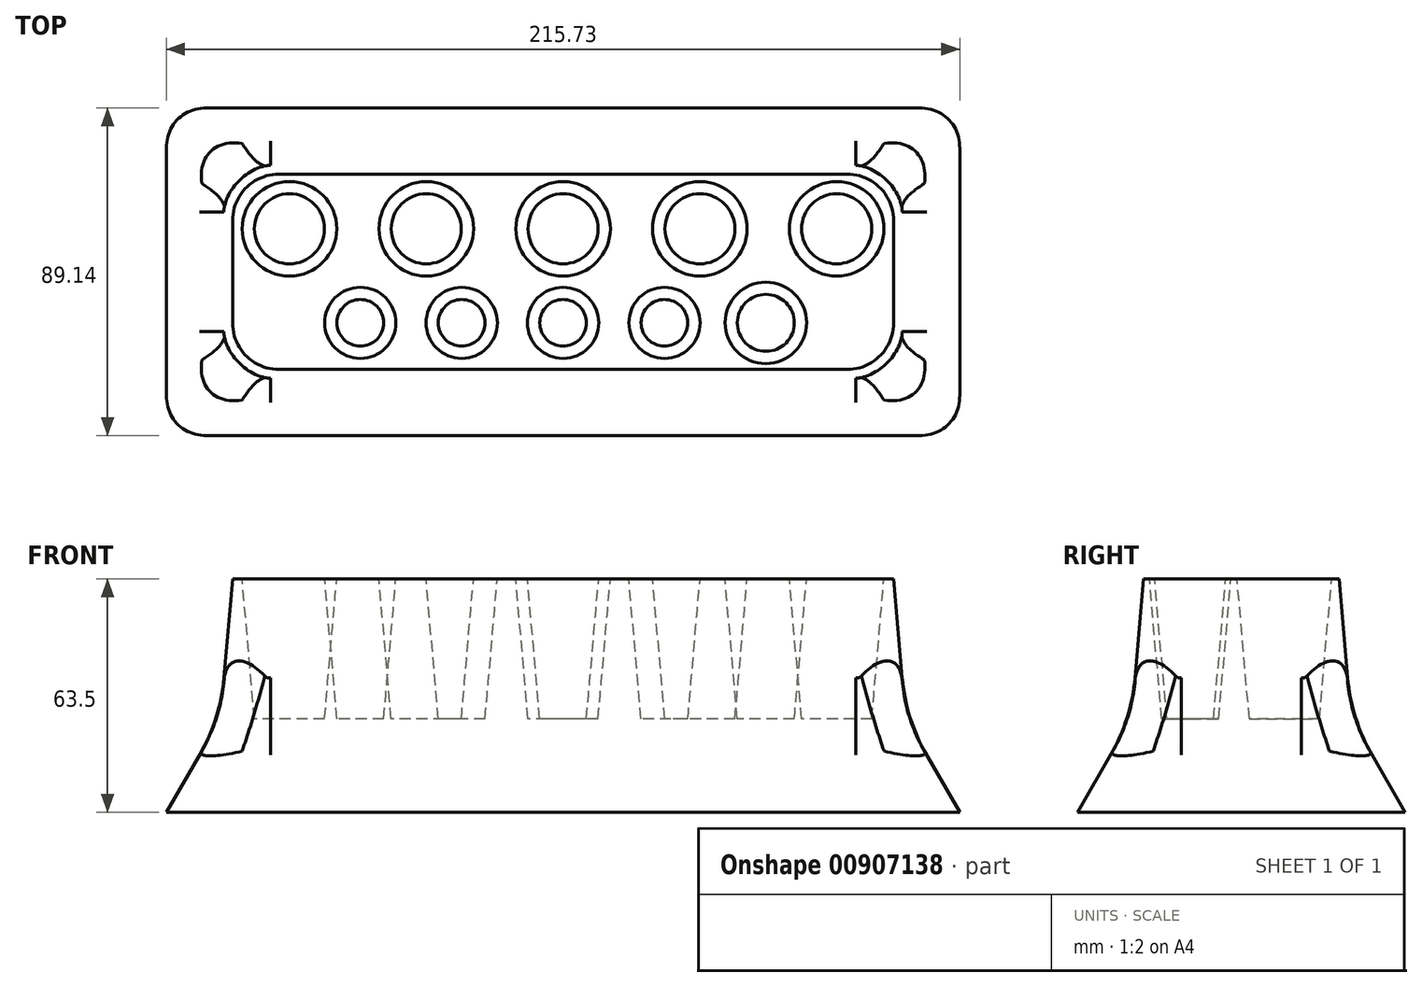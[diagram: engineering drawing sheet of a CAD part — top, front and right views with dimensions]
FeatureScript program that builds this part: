
annotation { "Feature Type Name" : "Feature", "Feature Type Description" : "" }
export const myFeature = defineFeature(function(context is Context, id is Id, definition is map)
    precondition{}
    {
        {
            var Q0;
            Q0=qCreatedBy(makeId("Top.planeOp"),FACE);
            var sketch = newSketch(context, id + "F0", { "sketchPlane" : qUnion([Q0])});
            skLineSegment(sketch, "E0.bottom", {"start": v(0, 0) * mm, "end": v(186.41, 0) * mm});
            skLineSegment(sketch, "E0.top", {"start": v(0, 59.81) * mm, "end": v(186.41, 59.81) * mm});
            skLineSegment(sketch, "E0.left", {"start": v(0, 0) * mm, "end": v(0, 59.81) * mm});
            skLineSegment(sketch, "E0.right", {"start": v(186.41, 0) * mm, "end": v(186.41, 59.81) * mm});
            skCircle(sketch, "E1", {"center": v(18.8, 41.6) * mm, "radius": 9.53 * mm});
            skCircle(sketch, "E2", {"center": v(56, 41.6) * mm, "radius": 9.53 * mm});
            skCircle(sketch, "E3", {"center": v(93.2, 41.6) * mm, "radius": 9.53 * mm});
            skCircle(sketch, "E4", {"center": v(130.4, 41.6) * mm, "radius": 9.53 * mm});
            skCircle(sketch, "E5", {"center": v(167.6, 41.6) * mm, "radius": 9.53 * mm});
            skCircle(sketch, "E6", {"center": v(38.08, 16) * mm, "radius": 6.35 * mm});
            skCircle(sketch, "E7", {"center": v(65.64, 16) * mm, "radius": 6.35 * mm});
            skCircle(sketch, "E8", {"center": v(93.2, 16) * mm, "radius": 6.35 * mm});
            skCircle(sketch, "E9", {"center": v(120.77, 16) * mm, "radius": 6.35 * mm});
            skCircle(sketch, "E10", {"center": v(148.33, 16) * mm, "radius": 7.75 * mm});
            skLineSegment(sketch, "E11", {"start": v(18.8, 41.6) * mm, "end": v(56, 41.6) * mm, "construction": true});
            skLineSegment(sketch, "E12", {"start": v(93.2, 41.6) * mm, "end": v(130.4, 41.6) * mm, "construction": true});
            skLineSegment(sketch, "E13", {"start": v(167.6, 41.6) * mm, "end": v(130.4, 41.6) * mm, "construction": true});
            skLineSegment(sketch, "E14", {"start": v(93.2, 41.6) * mm, "end": v(56, 41.6) * mm, "construction": true});
            skLineSegment(sketch, "E15", {"start": v(38.08, 16) * mm, "end": v(65.64, 16) * mm, "construction": true});
            skLineSegment(sketch, "E16", {"start": v(65.64, 16) * mm, "end": v(93.2, 16) * mm, "construction": true});
            skLineSegment(sketch, "E17", {"start": v(93.2, 16) * mm, "end": v(120.77, 16) * mm, "construction": true});
            skLineSegment(sketch, "E18", {"start": v(120.77, 16) * mm, "end": v(148.33, 16) * mm, "construction": true});
            skLineSegment(sketch, "E19", {"start": v(93.2, 41.6) * mm, "end": v(93.2, 16) * mm, "construction": true});
            skLineSegment(sketch, "E20", {"start": v(93.2, 0) * mm, "end": v(93.2, 16) * mm, "construction": true});
            skSolve(sketch);
        }
        {
            var Q0;
            Q0=makeQuery(id+"F0.imprint","IMPRINT",FACE,{"disambiguationData":[TD([[makeQuery(id+"F0.imprint","IMPRINT",EDGE,{"derivedFrom":sQuery(id+"F0.wireOp",EDGE,"E5")}),1.0]])]});
            var Q1;
            Q1=makeQuery(id+"F0.imprint","IMPRINT",FACE,{"disambiguationData":[TD([[makeQuery(id+"F0.imprint","IMPRINT",EDGE,{"derivedFrom":sQuery(id+"F0.wireOp",EDGE,"E0.bottom")}),1.0]])]});
            var Q2;
            Q2=makeQuery(id+"F0.imprint","IMPRINT",FACE,{"disambiguationData":[TD([[makeQuery(id+"F0.imprint","IMPRINT",EDGE,{"derivedFrom":sQuery(id+"F0.wireOp",EDGE,"E4")}),1.0]])]});
            var Q3;
            Q3=makeQuery(id+"F0.imprint","IMPRINT",FACE,{"disambiguationData":[TD([[makeQuery(id+"F0.imprint","IMPRINT",EDGE,{"derivedFrom":sQuery(id+"F0.wireOp",EDGE,"E10")}),1.0]])]});
            var Q4;
            Q4=makeQuery(id+"F0.imprint","IMPRINT",FACE,{"disambiguationData":[TD([[makeQuery(id+"F0.imprint","IMPRINT",EDGE,{"derivedFrom":sQuery(id+"F0.wireOp",EDGE,"E9")}),1.0]])]});
            var Q5;
            Q5=makeQuery(id+"F0.imprint","IMPRINT",FACE,{"disambiguationData":[TD([[makeQuery(id+"F0.imprint","IMPRINT",EDGE,{"derivedFrom":sQuery(id+"F0.wireOp",EDGE,"E3")}),1.0]])]});
            var Q6;
            Q6=makeQuery(id+"F0.imprint","IMPRINT",FACE,{"disambiguationData":[TD([[makeQuery(id+"F0.imprint","IMPRINT",EDGE,{"derivedFrom":sQuery(id+"F0.wireOp",EDGE,"E8")}),1.0]])]});
            var Q7;
            Q7=makeQuery(id+"F0.imprint","IMPRINT",FACE,{"disambiguationData":[TD([[makeQuery(id+"F0.imprint","IMPRINT",EDGE,{"derivedFrom":sQuery(id+"F0.wireOp",EDGE,"E2")}),1.0]])]});
            var Q8;
            Q8=makeQuery(id+"F0.imprint","IMPRINT",FACE,{"disambiguationData":[TD([[makeQuery(id+"F0.imprint","IMPRINT",EDGE,{"derivedFrom":sQuery(id+"F0.wireOp",EDGE,"E1")}),1.0]])]});
            var Q9;
            Q9=makeQuery(id+"F0.imprint","IMPRINT",FACE,{"disambiguationData":[TD([[makeQuery(id+"F0.imprint","IMPRINT",EDGE,{"derivedFrom":sQuery(id+"F0.wireOp",EDGE,"E6")}),1.0]])]});
            var Q10;
            Q10=makeQuery(id+"F0.imprint","IMPRINT",FACE,{"disambiguationData":[TD([[makeQuery(id+"F0.imprint","IMPRINT",EDGE,{"derivedFrom":sQuery(id+"F0.wireOp",EDGE,"E7")}),1.0]])]});
            extrude(context, id + "F1", {"entities" : qUnion([Q0, Q1, Q2, Q3, Q4, Q5, Q6, Q7, Q8, Q9, Q10]), "oppositeDirection" : true, "depth" : 25.4 * mm, "offsetDistance" : 25.4 * mm, "hasDraft" : true, "draftAngle" : 30 * degree});
        }
        {
            var Q0;
            Q0 = qSketchRegion(id + "F0", true);
            extrude(context, id + "F2", {"entities" : qUnion([Q0]), "operationType" : NewBodyOperationType.ADD, "depth" : 38.1 * mm, "offsetDistance" : 25.4 * mm, "hasDraft" : true, "draftAngle" : 5 * degree, "draftPullDirection" : true});
        }
        {
            var Q0;
            Q0=makeQuery(id+"F1.opExtrude","SWEPT_EDGE",EDGE,{"disambiguationData":[OSD([sQuery(id+"F0.wireOp",EDGE,"E0.bottom"),sQuery(id+"F0.wireOp",EDGE,"E0.right")])]});
            var Q1;
            Q1=makeQuery(id+"F2.opExtrude","SWEPT_EDGE",EDGE,{"disambiguationData":[OSD([sQuery(id+"F0.wireOp",EDGE,"E0.bottom"),sQuery(id+"F0.wireOp",EDGE,"E0.right")])]});
            var Q2;
            Q2=makeQuery(id+"F1.opExtrude","SWEPT_EDGE",EDGE,{"disambiguationData":[OSD([sQuery(id+"F0.wireOp",EDGE,"E0.top"),sQuery(id+"F0.wireOp",EDGE,"E0.right")])]});
            var Q3;
            Q3=makeQuery(id+"F2.opExtrude","SWEPT_EDGE",EDGE,{"disambiguationData":[OSD([sQuery(id+"F0.wireOp",EDGE,"E0.top"),sQuery(id+"F0.wireOp",EDGE,"E0.right")])]});
            var Q4;
            Q4=makeQuery(id+"F2.opExtrude","SWEPT_EDGE",EDGE,{"disambiguationData":[OSD([sQuery(id+"F0.wireOp",EDGE,"E0.bottom"),sQuery(id+"F0.wireOp",EDGE,"E0.left")])]});
            var Q5;
            Q5=makeQuery(id+"F1.opExtrude","SWEPT_EDGE",EDGE,{"disambiguationData":[OSD([sQuery(id+"F0.wireOp",EDGE,"E0.bottom"),sQuery(id+"F0.wireOp",EDGE,"E0.left")])]});
            var Q6;
            Q6=makeQuery(id+"F1.opExtrude","SWEPT_EDGE",EDGE,{"disambiguationData":[OSD([sQuery(id+"F0.wireOp",EDGE,"E0.top"),sQuery(id+"F0.wireOp",EDGE,"E0.left")])]});
            var Q7;
            Q7=makeQuery(id+"F2.opExtrude","SWEPT_EDGE",EDGE,{"disambiguationData":[OSD([sQuery(id+"F0.wireOp",EDGE,"E0.top"),sQuery(id+"F0.wireOp",EDGE,"E0.left")])]});
            fillet(context, id + "F3", {"entities" : qUnion([Q0, Q1, Q2, Q3, Q4, Q5, Q6, Q7]), "radius" : 12.7 * mm, "tangentPropagation" : true, "allowEdgeOverflow" : false});
        }
        {
            var Q0;
            {var subQ0=sQuery(id+"F0.wireOp",EDGE,"E0.bottom");Q0=makeQuery(id+"F2.boolean.opBoolean","MERGE",EDGE,{"derivedFrom":[makeQuery(id+"F1.opExtrude","CAP_EDGE",EDGE,{"disambiguationData":[OSD([subQ0])],"isStart":true}),makeQuery(id+"F2.opExtrude","CAP_EDGE",EDGE,{"disambiguationData":[OSD([subQ0])],"isStart":true})]});}
            var Q1;
            {var subQ0=sQuery(id+"F0.wireOp",EDGE,"E0.left");var subQ1=sQuery(id+"F0.wireOp",EDGE,"E0.bottom");Q1=makeQuery(id+"F3.opFillet","BLEND_EDGE",EDGE,{"blendedFrom":[makeQuery(id+"F1.opExtrude","SWEPT_EDGE",EDGE,{"disambiguationData":[OSD([subQ1,subQ0])]}),makeQuery(id+"F2.opExtrude","SWEPT_EDGE",EDGE,{"disambiguationData":[OSD([subQ1,subQ0])]})],"blendedInto":[]});}
            var Q2;
            {var subQ0=sQuery(id+"F0.wireOp",EDGE,"E0.left");Q2=makeQuery(id+"F2.boolean.opBoolean","MERGE",EDGE,{"derivedFrom":[makeQuery(id+"F1.opExtrude","CAP_EDGE",EDGE,{"disambiguationData":[OSD([subQ0])],"isStart":true}),makeQuery(id+"F2.opExtrude","CAP_EDGE",EDGE,{"disambiguationData":[OSD([subQ0])],"isStart":true})]});}
            var Q3;
            {var subQ0=sQuery(id+"F0.wireOp",EDGE,"E0.left");var subQ1=sQuery(id+"F0.wireOp",EDGE,"E0.top");Q3=makeQuery(id+"F3.opFillet","BLEND_EDGE",EDGE,{"blendedFrom":[makeQuery(id+"F1.opExtrude","SWEPT_EDGE",EDGE,{"disambiguationData":[OSD([subQ1,subQ0])]}),makeQuery(id+"F2.opExtrude","SWEPT_EDGE",EDGE,{"disambiguationData":[OSD([subQ1,subQ0])]})],"blendedInto":[]});}
            fillet(context, id + "F4", {"entities" : qUnion([Q0, Q1, Q2, Q3]), "radius" : 50.8 * mm, "tangentPropagation" : true, "allowEdgeOverflow" : false});
        }
    });
